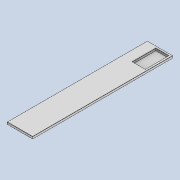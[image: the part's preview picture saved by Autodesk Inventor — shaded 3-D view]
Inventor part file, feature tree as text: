
AUTODESK INVENTOR PART (.ipt)
format: ipt  version: 2021 (Build 250183000, 183)  size: 244,224 bytes
history: native  units: mm
features: other x38, sketch x11, extrude x1
ambient origin geometry x8: Origin, YZ Plane, XZ Plane, XY Plane, X Axis, Y Axis, Z Axis, Center Point
bodies: Body1 (feature_tree)
feature tree (50):
  other  "Sólido1"
  other  "Cara1"
  other  "Pestaña1"
  other  "Pestaña2"
  other  "Pestaña3"
  other  "Pestaña4"
  extrude  "Extrusión1"  Depth=6600.0mm
  other  "Pestaña5"
  other  "Pestaña6"
  other  "Pestaña7"
  other  "Pestaña8"
  other  "Cara2"
  sketch  "Boceto1"  dims[d0=1200.0mm d1=6600.0mm]
  other  "Placa1"
  sketch  "Boceto2"  dims[d2=4.572mm]
  other  "Placa2"
  other  "Doblez1"
  other  "Esquina1"
  sketch  "Boceto3"  dims[d3=4.572mm]
  other  "Placa3"
  other  "Doblez2"
  other  "Esquina2"
  sketch  "Boceto4"  dims[d4=2.286mm]
  other  "Placa4"
  other  "Doblez3"
  other  "Esquina3"
  sketch  "Boceto5"  dims[d5=9.144mm]
  other  "Placa5"
  other  "Doblez4"
  other  "Esquina4"
  sketch  "Boceto6"  dims[d6=4.572mm]
  sketch  "Boceto7"  dims[d7=100.0mm d8=90.0deg d9=4.572mm]
  other  "Placa6"
  other  "Doblez5"
  other  "Esquina5"
  sketch  "Boceto8"  dims[d10=18.288mm]
  other  "Placa7"
  other  "Doblez6"
  other  "Esquina6"
  sketch  "Boceto9"  dims[d11=4.572mm]
  other  "Placa8"
  other  "Doblez7"
  other  "Esquina7"
  sketch  "Boceto10"  dims[d12=4.572mm]
  other  "Placa9"
  other  "Doblez8"
  other  "Esquina8"
  sketch  "Boceto11"  dims[d13=4.572mm d14=2.286mm d15=9.144mm d16=4.572mm d17=100.0mm d18=90.0deg d19=4.572mm d20=18.288mm d21=4.572mm d22=4.572mm d23=4.572mm d24=2.286mm d25=9.144mm d26=4.572mm d27=100.0mm d28=90.0deg d29=4.572mm d30=18.288mm d31=4.572mm d32=4.572mm d33=4.572mm d34=2.286mm d35=9.144mm d36=4.572mm d37=100.0mm d38=90.0deg d39=4.572mm d40=18.288mm d41=4.572mm d42=4.572mm d43=600.0mm d44=1100.0mm d45=0.0mm d46=0.0mm d47=4.572mm d48=2.286mm d49=9.144mm d50=4.572mm d51=100.0mm d52=90.0deg d53=4.572mm d54=18.288mm d55=4.572mm d56=4.572mm d57=4.572mm d58=2.286mm d59=9.144mm d60=4.572mm d61=100.0mm d62=90.0deg d63=4.572mm d64=18.288mm d65=4.572mm d66=4.572mm d67=4.572mm d68=2.286mm d69=9.144mm d70=4.572mm d71=100.0mm d72=90.0deg d73=4.572mm d74=18.288mm d75=4.572mm d76=4.572mm d77=4.572mm d78=2.286mm d79=9.144mm d80=4.572mm d81=100.0mm d82=90.0deg d83=4.572mm d84=18.288mm d85=4.572mm d86=4.572mm d87=4.572mm d88=4.572mm d89=2.286mm d90=9.144mm d91=4.572mm]
  other  "Placa10"
  other  "Doblez9"
